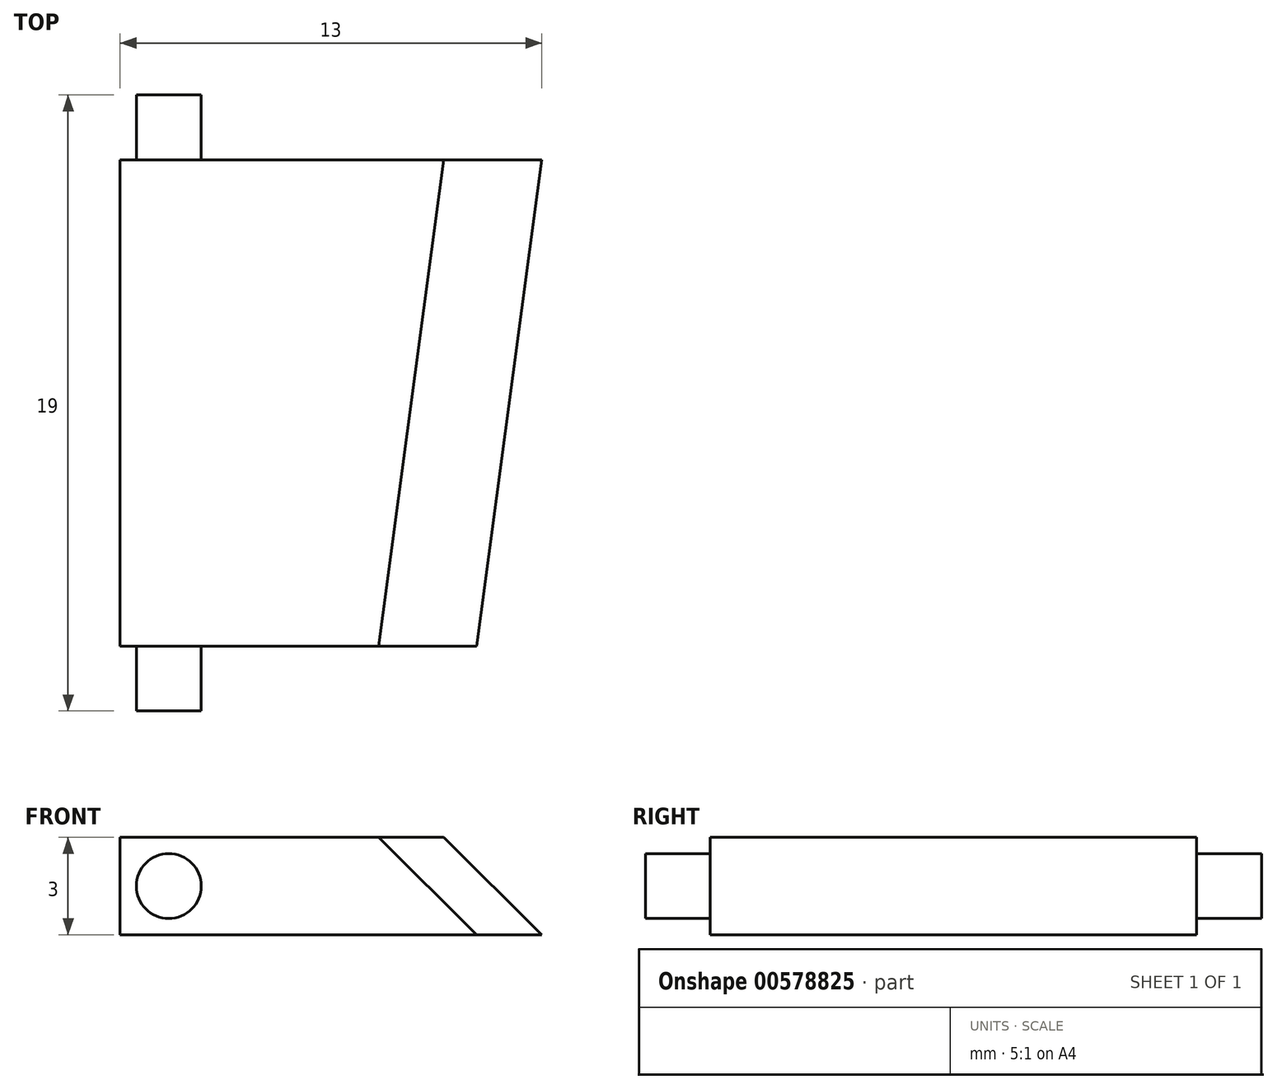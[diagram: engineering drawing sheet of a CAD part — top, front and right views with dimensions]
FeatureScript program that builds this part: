
annotation { "Feature Type Name" : "Feature", "Feature Type Description" : "" }
export const myFeature = defineFeature(function(context is Context, id is Id, definition is map)
    precondition{}
    {
        {
            var Q0;
            Q0=qCreatedBy(makeId("Top.planeOp"),FACE);
            var sketch = newSketch(context, id + "F0", { "sketchPlane" : qUnion([Q0])});
            skLineSegment(sketch, "E0", {"start": v(0, 0) * mm, "end": v(22, 0) * mm});
            skLineSegment(sketch, "E1", {"start": v(0, 15) * mm, "end": v(24, 15) * mm});
            skLineSegment(sketch, "E2", {"start": v(24, 15) * mm, "end": v(22, 0) * mm});
            skLineSegment(sketch, "E3", {"start": v(11, 0) * mm, "end": v(11, 15) * mm});
            skLineSegment(sketch, "E4", {"start": v(11, 15) * mm, "end": v(11, 12) * mm});
            skLineSegment(sketch, "E5", {"start": v(11, 12) * mm, "end": v(0, 12) * mm});
            skLineSegment(sketch, "E6", {"start": v(11, 3) * mm, "end": v(0, 3) * mm});
            skLineSegment(sketch, "E7", {"start": v(11, 3) * mm, "end": v(11, 0) * mm});
            skLineSegment(sketch, "E8", {"start": v(0, 12) * mm, "end": v(0, 3) * mm});
            skSolve(sketch);
        }
        {
            var Q0;
            Q0=makeQuery(id+"F0.imprint","IMPRINT",FACE,{"disambiguationData":[TD([[makeQuery(id+"F0.imprint","IMPRINT",EDGE,{"derivedFrom":sQuery(id+"F0.wireOp",EDGE,"E0")}),1.0]])]});
            extrude(context, id + "F1", {"entities" : qUnion([Q0]), "depth" : 3 * mm, "offsetDistance" : 25 * mm});
        }
        {
            var Q0;
            Q0=makeQuery(id+"F1.opExtrude","CAP_EDGE",EDGE,{"disambiguationData":[OSD([sQuery(id+"F0.wireOp",EDGE,"E2")])],"isStart":false});
            chamfer(context, id + "F2", {"entities" : qUnion([Q0]), "chamferType" : ChamferType.TWO_OFFSETS, "width1" : 3 * mm, "oppositeDirection" : false, "width2" : 3 * mm, "tangentPropagation" : true});
        }
        {
            var Q0;
            Q0=makeQuery(id+"F1.opExtrude","SWEPT_FACE",FACE,{"disambiguationData":[OSD([sQuery(id+"F0.wireOp",EDGE,"E0")])]});
            var sketch = newSketch(context, id + "F3", { "sketchPlane" : qUnion([Q0])});
            skCircle(sketch, "E9", {"center": v(12.5, 1.5) * mm, "radius": 1 * mm});
            skPoint(sketch, "E9.centerSnap0", {"position": v(11, 1.5) * mm});
            skSolve(sketch);
        }
        {
            var Q0;
            Q0=makeQuery(id+"F3.imprint","IMPRINT",FACE,{"disambiguationData":[TD([[makeQuery(id+"F3.imprint","IMPRINT",EDGE,{"derivedFrom":sQuery(id+"F3.wireOp",EDGE,"E9")}),1.0]])]});
            extrude(context, id + "F4", {"entities" : qUnion([Q0]), "operationType" : NewBodyOperationType.ADD, "depth" : 2 * mm, "offsetDistance" : 25 * mm});
        }
        {
            var Q0;
            Q0=makeQuery(id+"F1.opExtrude","SWEPT_FACE",FACE,{"disambiguationData":[OSD([sQuery(id+"F0.wireOp",EDGE,"E1")])]});
            var sketch = newSketch(context, id + "F5", { "sketchPlane" : qUnion([Q0])});
            skCircle(sketch, "E10", {"center": v(-12.5, 1.5) * mm, "radius": 1 * mm});
            skPoint(sketch, "E10.centerSnap0", {"position": v(-11, 1.5) * mm});
            skSolve(sketch);
        }
        {
            var Q0;
            Q0=makeQuery(id+"F5.imprint","IMPRINT",FACE,{"disambiguationData":[TD([[makeQuery(id+"F5.imprint","IMPRINT",EDGE,{"derivedFrom":sQuery(id+"F5.wireOp",EDGE,"E10")}),1.0]])]});
            extrude(context, id + "F6", {"entities" : qUnion([Q0]), "operationType" : NewBodyOperationType.ADD, "depth" : 2 * mm, "offsetDistance" : 25 * mm});
        }
    });
